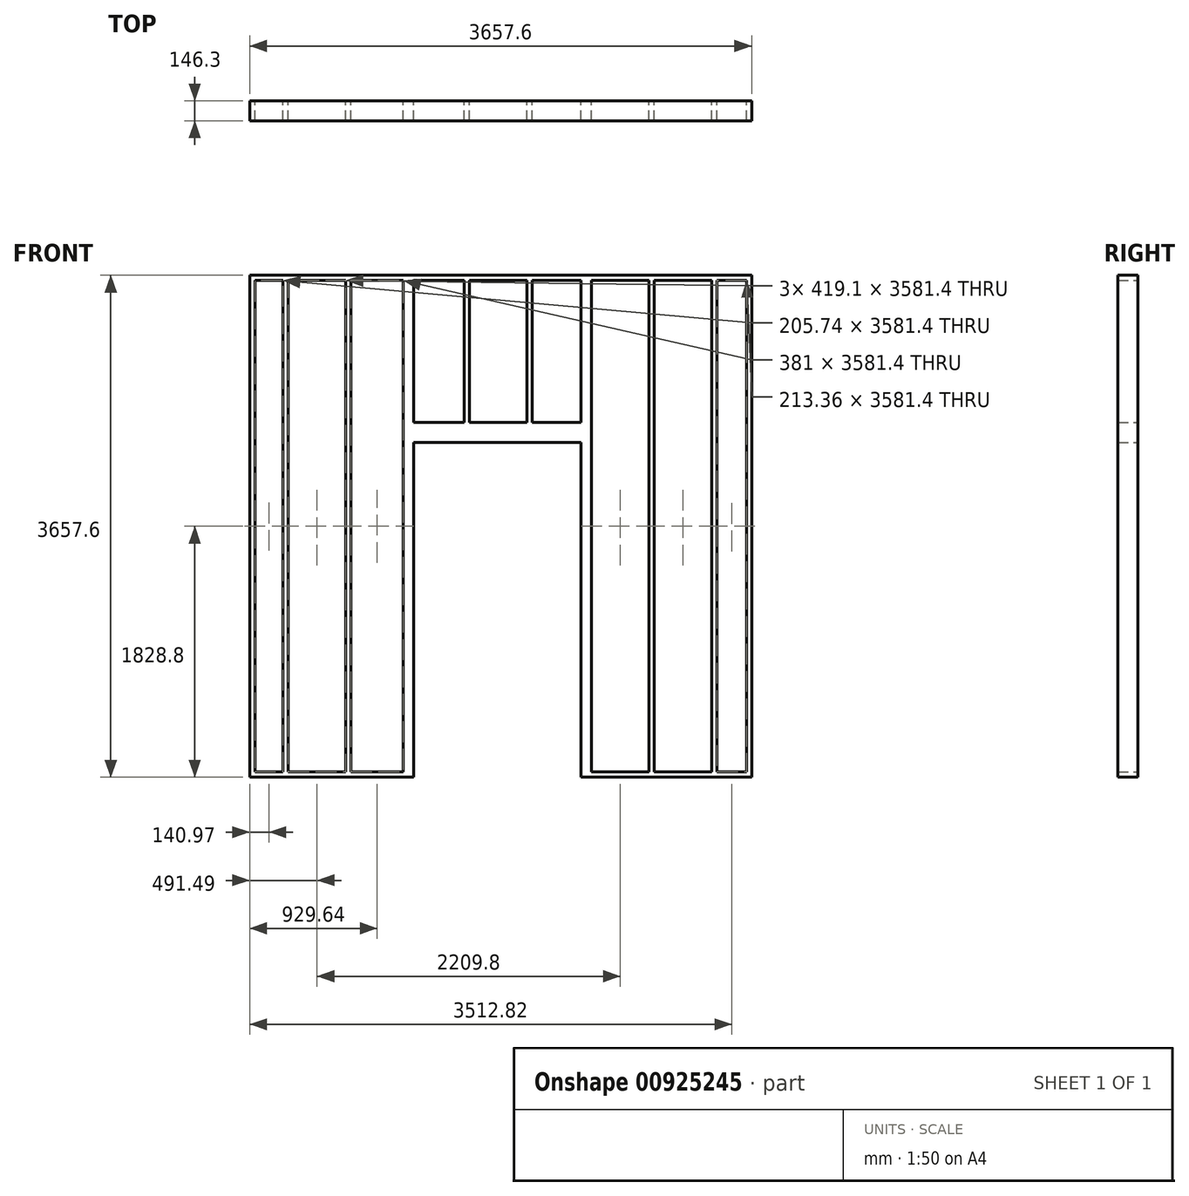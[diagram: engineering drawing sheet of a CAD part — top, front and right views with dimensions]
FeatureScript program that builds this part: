
annotation { "Feature Type Name" : "Feature", "Feature Type Description" : "" }
export const myFeature = defineFeature(function(context is Context, id is Id, definition is map)
    precondition{}
    {
        {
            var Q0;
            Q0=qCreatedBy(makeId("Front.planeOp"),FACE);
            var sketch = newSketch(context, id + "F0", { "sketchPlane" : qUnion([Q0])});
            skLineSegment(sketch, "E0.bottom", {"start": v(457.2, 0) * mm, "end": v(1653.54, 0) * mm});
            skLineSegment(sketch, "E0.top", {"start": v(457.2, 3657.6) * mm, "end": v(4114.8, 3657.6) * mm});
            skLineSegment(sketch, "E1.8.0.0", {"start": v(457.2, 3619.5) * mm, "end": v(457.2, 38.1) * mm});
            skLineSegment(sketch, "E1.8.0.1", {"start": v(495.3, 3619.5) * mm, "end": v(495.3, 38.1) * mm});
            skLineSegment(sketch, "E1.9.0.0", {"start": v(701.04, 3619.5) * mm, "end": v(701.04, 38.1) * mm});
            skLineSegment(sketch, "E1.9.0.1", {"start": v(739.14, 3619.5) * mm, "end": v(739.14, 38.1) * mm});
            skLineSegment(sketch, "E1.10.0.0", {"start": v(1158.24, 3619.5) * mm, "end": v(1158.24, 38.1) * mm});
            skLineSegment(sketch, "E1.10.0.1", {"start": v(1196.34, 3619.5) * mm, "end": v(1196.34, 38.1) * mm});
            skLineSegment(sketch, "E1.11.0.0", {"start": v(1577.34, 3619.5) * mm, "end": v(1577.34, 38.1) * mm});
            skLineSegment(sketch, "E1.11.0.1", {"start": v(1653.54, 3619.5) * mm, "end": v(1653.54, 2584.7) * mm});
            skLineSegment(sketch, "E1.12.0.0", {"start": v(2019.3, 3619.5) * mm, "end": v(2019.3, 2584.7) * mm});
            skLineSegment(sketch, "E1.12.0.1", {"start": v(2057.4, 3619.5) * mm, "end": v(2057.4, 2584.7) * mm});
            skLineSegment(sketch, "E1.13.0.0", {"start": v(2476.5, 3619.5) * mm, "end": v(2476.5, 2584.7) * mm});
            skLineSegment(sketch, "E1.13.0.1", {"start": v(2514.6, 3619.5) * mm, "end": v(2514.6, 2584.7) * mm});
            skLineSegment(sketch, "E1.14.0.0", {"start": v(2872.74, 3619.5) * mm, "end": v(2872.74, 2584.7) * mm});
            skLineSegment(sketch, "E1.14.0.1", {"start": v(2948.94, 3619.5) * mm, "end": v(2948.94, 38.1) * mm});
            skLineSegment(sketch, "E1.15.0.0", {"start": v(3368.04, 3619.5) * mm, "end": v(3368.04, 38.1) * mm});
            skLineSegment(sketch, "E1.15.0.1", {"start": v(3406.14, 3619.5) * mm, "end": v(3406.14, 38.1) * mm});
            skLineSegment(sketch, "E1.16.0.0", {"start": v(3825.24, 3619.5) * mm, "end": v(3825.24, 38.1) * mm});
            skLineSegment(sketch, "E1.16.0.1", {"start": v(3863.34, 3619.5) * mm, "end": v(3863.34, 38.1) * mm});
            skLineSegment(sketch, "E1.17.0.0", {"start": v(4076.7, 3619.5) * mm, "end": v(4076.7, 38.1) * mm});
            skLineSegment(sketch, "E1.17.0.1", {"start": v(4114.8, 3619.5) * mm, "end": v(4114.8, 38.1) * mm});
            skLineSegment(sketch, "E2.trimOffspring", {"start": v(495.3, 3619.5) * mm, "end": v(701.04, 3619.5) * mm});
            skLineSegment(sketch, "E3.trimOffspring", {"start": v(739.14, 3619.5) * mm, "end": v(1158.24, 3619.5) * mm});
            skLineSegment(sketch, "E4.trimOffspring", {"start": v(1196.34, 3619.5) * mm, "end": v(1577.34, 3619.5) * mm});
            skLineSegment(sketch, "E5.trimOffspring", {"start": v(1653.54, 3619.5) * mm, "end": v(2019.3, 3619.5) * mm});
            skLineSegment(sketch, "E6.trimOffspring", {"start": v(2057.4, 3619.5) * mm, "end": v(2476.5, 3619.5) * mm});
            skLineSegment(sketch, "E7.trimOffspring", {"start": v(2514.6, 3619.5) * mm, "end": v(2872.74, 3619.5) * mm});
            skLineSegment(sketch, "E8.trimOffspring", {"start": v(2948.94, 3619.5) * mm, "end": v(3368.04, 3619.5) * mm});
            skLineSegment(sketch, "E9.trimOffspring", {"start": v(3406.14, 3619.5) * mm, "end": v(3825.24, 3619.5) * mm});
            skLineSegment(sketch, "E10.trimOffspring", {"start": v(3863.34, 3619.5) * mm, "end": v(4076.7, 3619.5) * mm});
            skLineSegment(sketch, "E11.trimOffspring", {"start": v(3863.34, 38.1) * mm, "end": v(4076.7, 38.1) * mm});
            skLineSegment(sketch, "E12.trimOffspring", {"start": v(3406.14, 38.1) * mm, "end": v(3825.24, 38.1) * mm});
            skLineSegment(sketch, "E13.trimOffspring", {"start": v(2948.94, 38.1) * mm, "end": v(3368.04, 38.1) * mm});
            skLineSegment(sketch, "E14.trimOffspring", {"start": v(1196.34, 38.1) * mm, "end": v(1577.34, 38.1) * mm});
            skLineSegment(sketch, "E15.trimOffspring", {"start": v(739.14, 38.1) * mm, "end": v(1158.24, 38.1) * mm});
            skLineSegment(sketch, "E16.trimOffspring", {"start": v(495.3, 38.1) * mm, "end": v(701.04, 38.1) * mm});
            skLineSegment(sketch, "E17.bottom", {"start": v(1653.54, 2438.4) * mm, "end": v(2019.3, 2438.4) * mm});
            skLineSegment(sketch, "E17.left", {"start": v(1653.54, 2438.4) * mm, "end": v(1653.54, 1219.2) * mm});
            skLineSegment(sketch, "E17.right", {"start": v(2872.74, 2438.4) * mm, "end": v(2872.74, 1219.2) * mm});
            skLineSegment(sketch, "E18.trimOffspring", {"start": v(1653.54, 1072.9) * mm, "end": v(1653.54, 38.1) * mm});
            skLineSegment(sketch, "E19.trimOffspring", {"start": v(2872.74, 1072.9) * mm, "end": v(2872.74, 38.1) * mm});
            skLineSegment(sketch, "E20", {"start": v(1653.54, 2584.7) * mm, "end": v(2019.3, 2584.7) * mm});
            skLineSegment(sketch, "E21.trimOffspring", {"start": v(2057.4, 2584.7) * mm, "end": v(2476.5, 2584.7) * mm});
            skLineSegment(sketch, "E22.trimOffspring", {"start": v(2514.6, 2584.7) * mm, "end": v(2872.74, 2584.7) * mm});
            skLineSegment(sketch, "E23.trimOffspring", {"start": v(2019.3, 2438.4) * mm, "end": v(2514.6, 2438.4) * mm});
            skLineSegment(sketch, "E24.trimOffspring", {"start": v(2514.6, 2438.4) * mm, "end": v(2872.74, 2438.4) * mm});
            skLineSegment(sketch, "E25", {"start": v(2019.3, 2438.4) * mm, "end": v(2476.5, 2438.4) * mm});
            skLineSegment(sketch, "E26", {"start": v(457.2, 3619.5) * mm, "end": v(457.2, 3657.6) * mm});
            skLineSegment(sketch, "E27", {"start": v(457.2, 38.1) * mm, "end": v(457.2, 0) * mm});
            skLineSegment(sketch, "E28", {"start": v(4114.8, 3619.5) * mm, "end": v(4114.8, 3657.6) * mm});
            skLineSegment(sketch, "E29", {"start": v(4114.8, 38.1) * mm, "end": v(4114.8, 0) * mm});
            skLineSegment(sketch, "E30", {"start": v(1653.54, 38.1) * mm, "end": v(1653.54, 0) * mm});
            skLineSegment(sketch, "E31", {"start": v(2872.74, 38.1) * mm, "end": v(2872.74, 0) * mm});
            skLineSegment(sketch, "E32", {"start": v(1653.54, 1219.2) * mm, "end": v(1653.54, 1072.9) * mm});
            skLineSegment(sketch, "E33", {"start": v(2872.74, 1219.2) * mm, "end": v(2872.74, 1072.9) * mm});
            skLineSegment(sketch, "E34.trimOffspring", {"start": v(2872.74, 0) * mm, "end": v(4114.8, 0) * mm});
            skSolve(sketch);
        }
        {
            var Q0;
            Q0=qSketchRegion(id+"F0",true);
            extrude(context, id + "F1", {"entities" : qUnion([Q0]), "depth" : 146.3 * mm, "offsetDistance" : 30.48 * mm});
        }
    });
